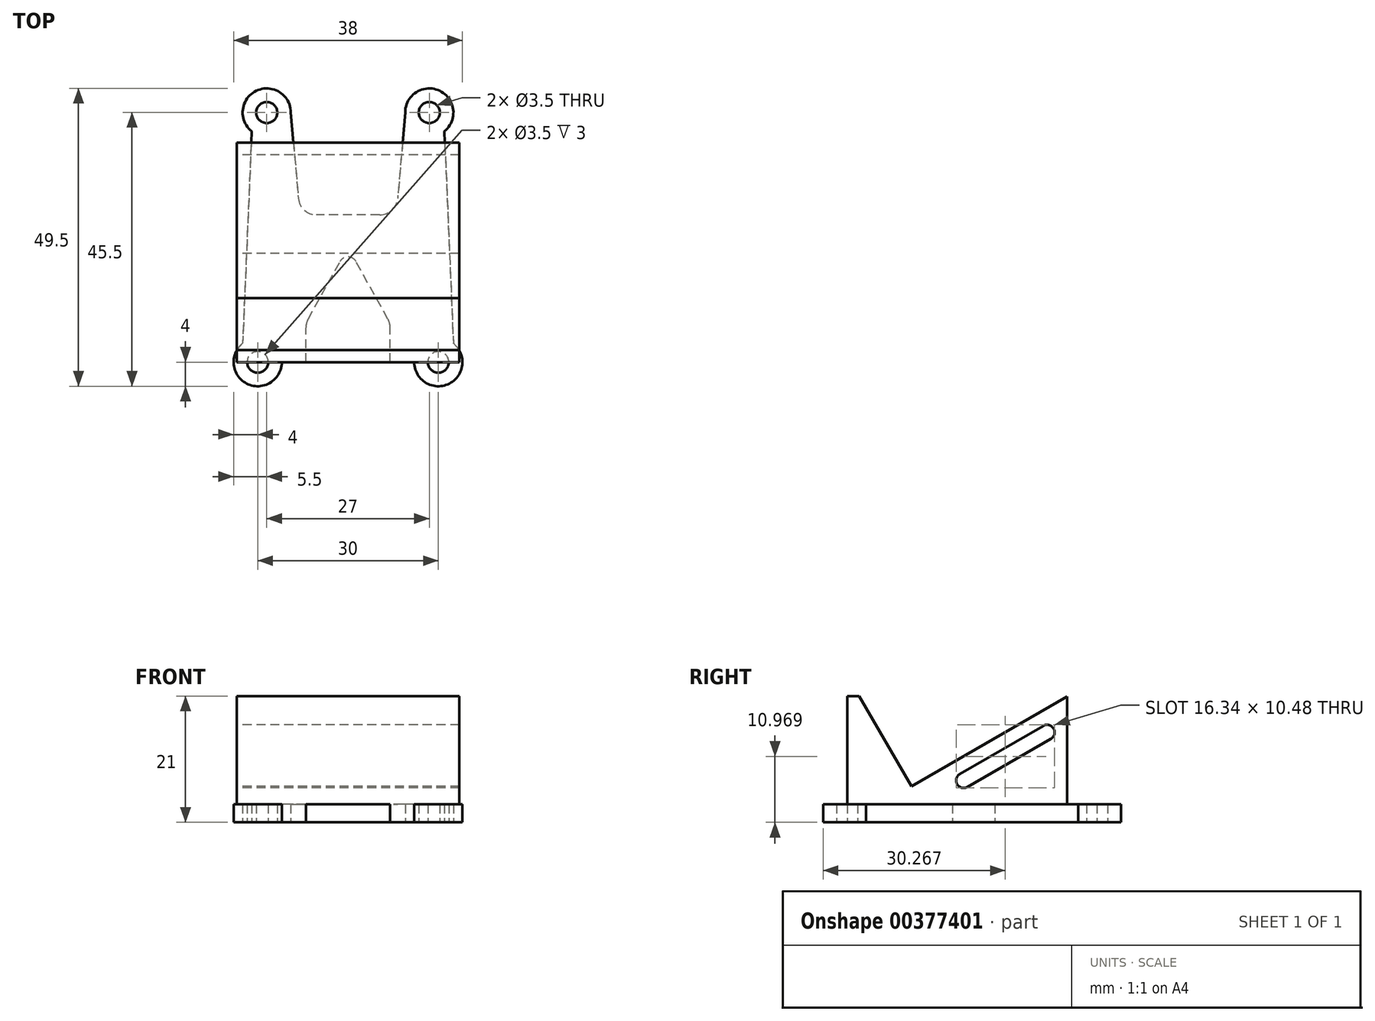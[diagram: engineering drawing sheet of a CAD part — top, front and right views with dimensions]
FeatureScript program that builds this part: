
annotation { "Feature Type Name" : "Feature", "Feature Type Description" : "" }
export const myFeature = defineFeature(function(context is Context, id is Id, definition is map)
    precondition{}
    {
        {
            var Q0;
            Q0=qCreatedBy(makeId("Top.planeOp"),FACE);
            var sketch = newSketch(context, id + "F0", { "sketchPlane" : qUnion([Q0])});
            skCircle(sketch, "E0", {"center": v(-15, -20.75) * mm, "radius": 1.75 * mm});
            skCircle(sketch, "E1", {"center": v(-13.5, 20.75) * mm, "radius": 1.75 * mm});
            skCircle(sketch, "E2.MirrorC", {"center": v(13.5, 20.75) * mm, "radius": 1.75 * mm});
            skCircle(sketch, "E3.MirrorC", {"center": v(15, -20.75) * mm, "radius": 1.75 * mm});
            skLineSegment(sketch, "E4", {"start": v(9.5, 20.75) * mm, "end": v(8.24, 6.49) * mm});
            skLineSegment(sketch, "E5", {"start": v(5.25, 3.75) * mm, "end": v(0, 3.75) * mm});
            skLineSegment(sketch, "E6.MirrorCS", {"start": v(-9.5, 20.75) * mm, "end": v(-8.24, 6.49) * mm});
            skLineSegment(sketch, "E7.MirrorCS", {"start": v(-5.25, 3.75) * mm, "end": v(0, 3.75) * mm});
            skArc(sketch, "E8", {"start": v(-9.5, 20.75) * mm, "mid": v(-15.23, 24.36) * mm, "end": v(-16, 17.63) * mm});
            skArc(sketch, "E9", {"start": v(16, 17.63) * mm, "mid": v(15.23, 24.36) * mm, "end": v(9.5, 20.75) * mm});
            skArc(sketch, "E10", {"start": v(1.31, -4.02) * mm, "mid": v(0, -3.25) * mm, "end": v(-1.31, -4.02) * mm});
            skPoint(sketch, "E11.visualSharp", {"position": v(-8, 3.75) * mm});
            skArc(sketch, "E11.filletArc", {"start": v(-8.24, 6.49) * mm, "mid": v(-7.28, 4.54) * mm, "end": v(-5.25, 3.75) * mm});
            skPoint(sketch, "E12.visualSharp", {"position": v(8, 3.75) * mm});
            skArc(sketch, "E12.filletArc", {"start": v(5.25, 3.75) * mm, "mid": v(7.28, 4.54) * mm, "end": v(8.24, 6.49) * mm});
            skLineSegment(sketch, "E13", {"start": v(-7, -20.75) * mm, "end": v(-7, -15.03) * mm});
            skLineSegment(sketch, "E14", {"start": v(-6.62, -13.57) * mm, "end": v(-1.31, -4.02) * mm});
            skLineSegment(sketch, "E15.MirrorCS", {"start": v(6.62, -13.57) * mm, "end": v(1.31, -4.02) * mm});
            skLineSegment(sketch, "E16.MirrorCS", {"start": v(7, -20.75) * mm, "end": v(7, -15.03) * mm});
            skArc(sketch, "E17", {"start": v(-17.5, -17.63) * mm, "mid": v(-16.73, -24.36) * mm, "end": v(-11, -20.75) * mm});
            skArc(sketch, "E18.MirrorC", {"start": v(17.5, -17.63) * mm, "mid": v(16.73, -24.36) * mm, "end": v(11, -20.75) * mm});
            skLineSegment(sketch, "E19", {"start": v(-11, -20.75) * mm, "end": v(-7, -20.75) * mm});
            skLineSegment(sketch, "E20.trimOffspring", {"start": v(7, -20.75) * mm, "end": v(11, -20.75) * mm});
            skLineSegment(sketch, "E21", {"start": v(-16, 17.63) * mm, "end": v(-17.5, -17.63) * mm});
            skLineSegment(sketch, "E22.MirrorCS", {"start": v(16, 17.63) * mm, "end": v(17.5, -17.63) * mm});
            skPoint(sketch, "E23.visualSharp", {"position": v(-7, -14.25) * mm});
            skArc(sketch, "E23.filletArc", {"start": v(-6.62, -13.57) * mm, "mid": v(-6.9, -14.27) * mm, "end": v(-7, -15.03) * mm});
            skPoint(sketch, "E24.visualSharp", {"position": v(7, -14.25) * mm});
            skArc(sketch, "E24.filletArc", {"start": v(7, -15.03) * mm, "mid": v(6.9, -14.27) * mm, "end": v(6.62, -13.57) * mm});
            skSolve(sketch);
        }
        {
            var Q0;
            Q0 = qSketchRegion(id + "F0", true);
            extrude(context, id + "F1", {"entities" : qUnion([Q0]), "depth" : 3 * mm});
        }
        {
            var Q0;
            Q0=qCreatedBy(makeId("Right.planeOp"),FACE);
            var sketch = newSketch(context, id + "F2", { "sketchPlane" : qUnion([Q0])});
            skLineSegment(sketch, "E25.bottom", {"start": v(-20.75, 3) * mm, "end": v(15.75, 3) * mm});
            skLineSegment(sketch, "E25.top", {"start": v(-20.75, 21) * mm, "end": v(-18.75, 21) * mm});
            skLineSegment(sketch, "E25.left", {"start": v(-20.75, 3) * mm, "end": v(-20.75, 21) * mm});
            skLineSegment(sketch, "E25.right", {"start": v(15.75, 3) * mm, "end": v(15.75, 20.92) * mm});
            skLineSegment(sketch, "E26", {"start": v(15.75, 20.92) * mm, "end": v(-10.09, 6) * mm});
            skLineSegment(sketch, "E27", {"start": v(-10.09, 6) * mm, "end": v(-18.75, 21) * mm});
            skLineSegment(sketch, "E28", {"start": v(12.44, 14.97) * mm, "end": v(-1.41, 6.97) * mm, "construction": true});
            skArc(sketch, "E29.0.startCap", {"start": v(11.82, 16.05) * mm, "mid": v(13.53, 15.6) * mm, "end": v(13.07, 13.89) * mm});
            skArc(sketch, "E29.0.endCap", {"start": v(-0.79, 5.89) * mm, "mid": v(-2.5, 6.34) * mm, "end": v(-2.04, 8.05) * mm});
            skLineSegment(sketch, "E29.0.left", {"start": v(13.07, 13.89) * mm, "end": v(-0.79, 5.89) * mm});
            skLineSegment(sketch, "E29.0.right", {"start": v(11.82, 16.05) * mm, "end": v(-2.04, 8.05) * mm});
            skSolve(sketch);
        }
        {
            var Q0;
            Q0=makeQuery(id+"F2.imprint","IMPRINT",FACE,{"disambiguationData":[TD([[makeQuery(id+"F2.imprint","IMPRINT",EDGE,{"derivedFrom":sQuery(id+"F2.wireOp",EDGE,"E25.bottom")}),1.0]])]});
            extrude(context, id + "F3", {"entities" : qUnion([Q0]), "operationType" : NewBodyOperationType.ADD, "endBound" : BoundingType.SYMMETRIC, "depth" : 37 * mm});
        }
    });
